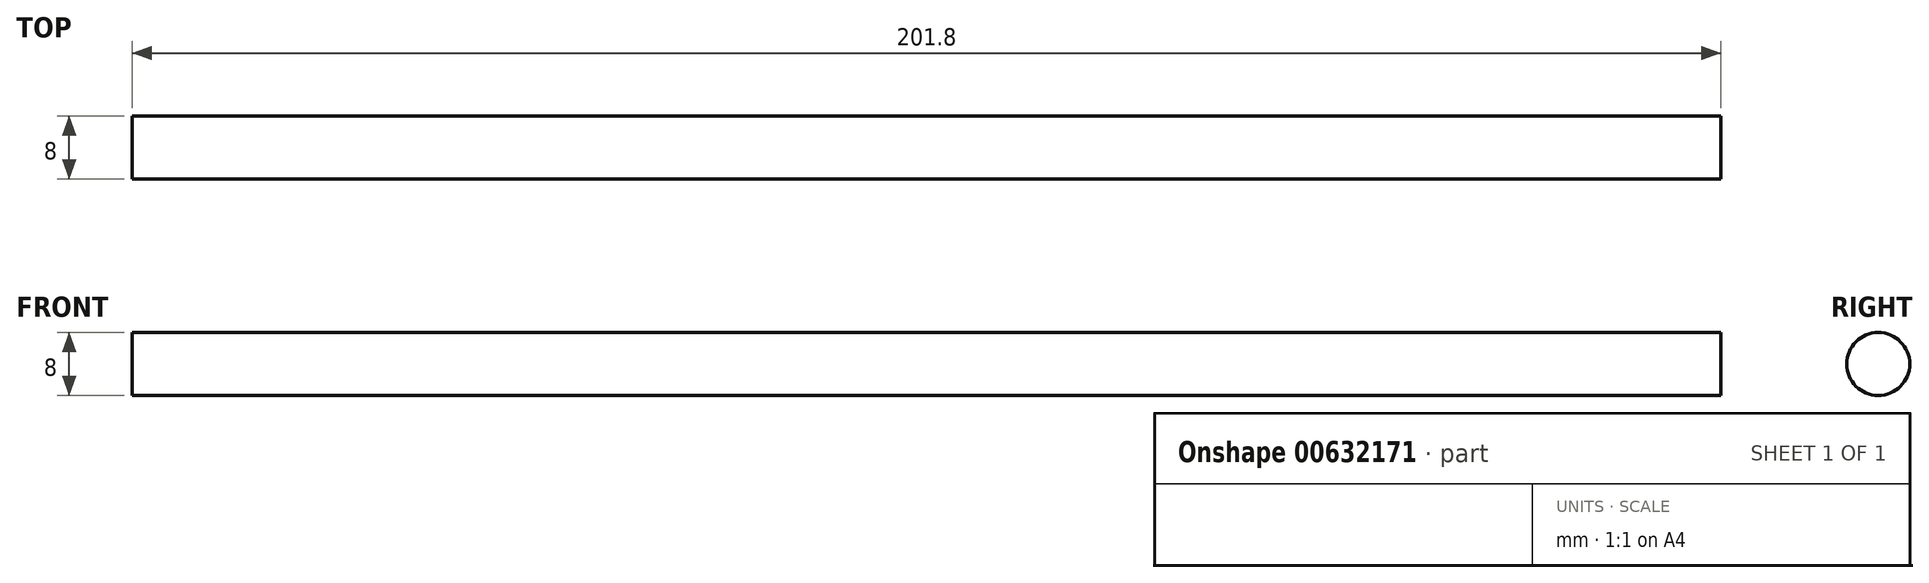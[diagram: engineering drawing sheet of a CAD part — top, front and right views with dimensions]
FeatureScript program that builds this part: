
annotation { "Feature Type Name" : "Feature", "Feature Type Description" : "" }
export const myFeature = defineFeature(function(context is Context, id is Id, definition is map)
    precondition{}
    {
        {
            var Q0;
            Q0=qCreatedBy(makeId("Right.planeOp"),FACE);
            var sketch = newSketch(context, id + "F0", { "sketchPlane" : qUnion([Q0])});
            skCircle(sketch, "E0", {"center": v(0, 0) * mm, "radius": 4 * mm});
            skSolve(sketch);
        }
        {
            var Q0;
            Q0 = qSketchRegion(id + "F0", true);
            extrude(context, id + "F1", {"entities" : qUnion([Q0]), "depth" : 201.8 * mm, "offsetDistance" : 25 * mm});
        }
    });
